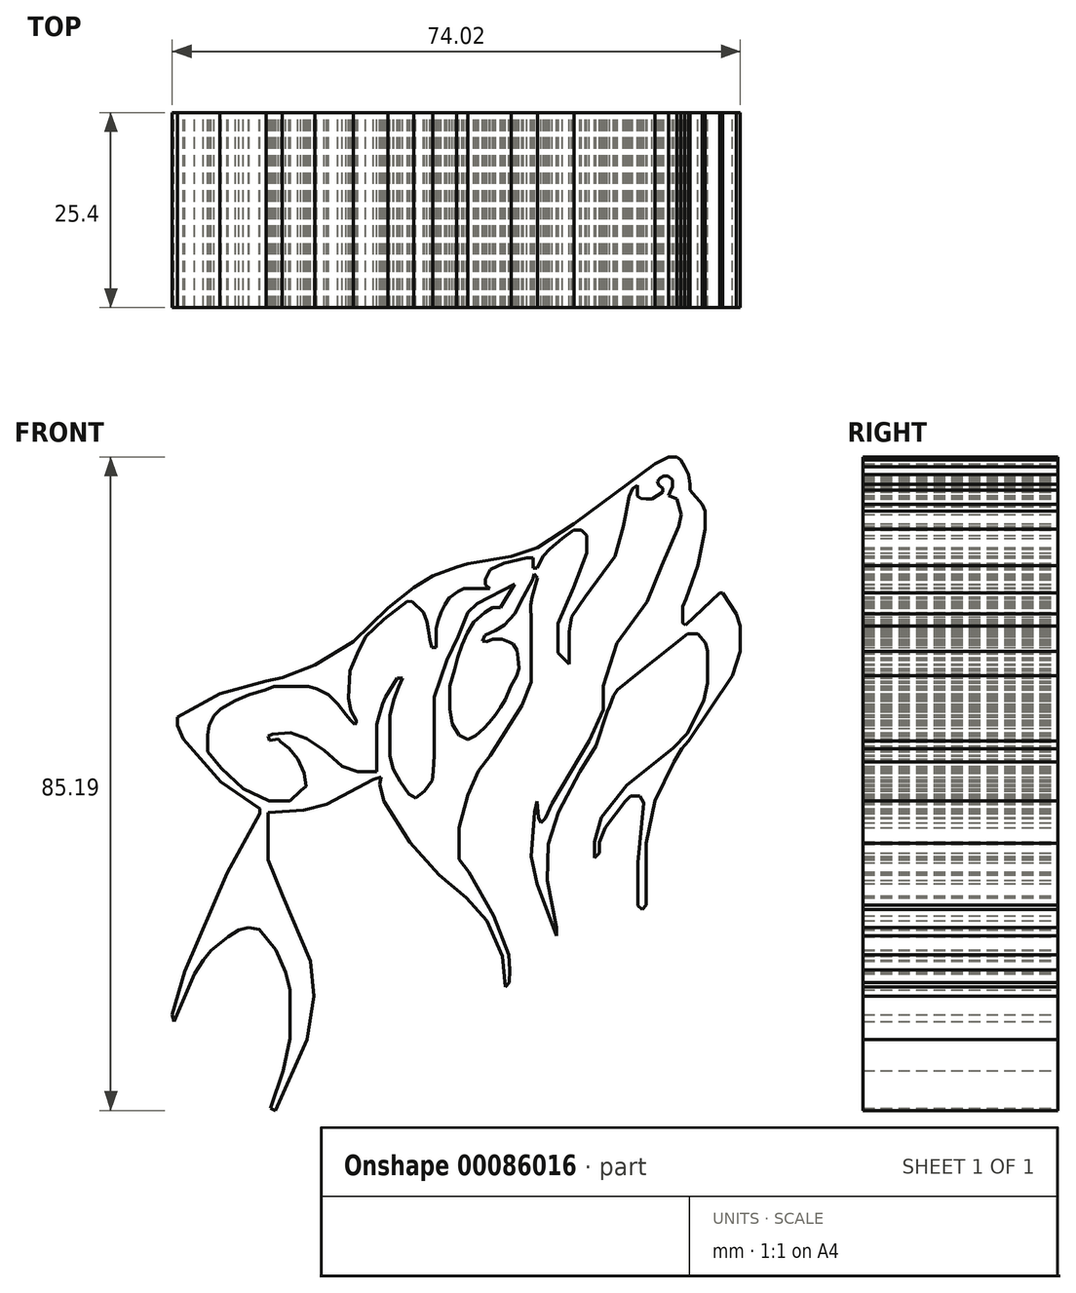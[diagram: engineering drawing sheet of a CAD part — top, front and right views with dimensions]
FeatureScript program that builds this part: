
annotation { "Feature Type Name" : "Feature", "Feature Type Description" : "" }
export const myFeature = defineFeature(function(context is Context, id is Id, definition is map)
    precondition{}
    {
        {
            var Q0;
            Q0=qCreatedBy(makeId("Front.planeOp"),FACE);
            var sketch = newSketch(context, id + "F0", { "sketchPlane" : qUnion([Q0])});
            skLineSegment(sketch, "E0", {"start": v(-38.5, -15.53) * mm, "end": v(-36.88, -9.84) * mm});
            skLineSegment(sketch, "E1", {"start": v(-36.88, -9.84) * mm, "end": v(-31.3, 2.95) * mm});
            skLineSegment(sketch, "E2", {"start": v(-31.3, 2.95) * mm, "end": v(-27.1, 10.73) * mm});
            skLineSegment(sketch, "E3", {"start": v(-27.1, 10.73) * mm, "end": v(-27.1, 11.36) * mm});
            skLineSegment(sketch, "E4", {"start": v(-27.1, 11.36) * mm, "end": v(-32.14, 14.82) * mm});
            skLineSegment(sketch, "E5", {"start": v(-32.14, 14.82) * mm, "end": v(-37.06, 20.41) * mm});
            skLineSegment(sketch, "E6", {"start": v(-37.06, 20.41) * mm, "end": v(-37.8, 22.21) * mm});
            skLineSegment(sketch, "E7", {"start": v(-37.8, 22.21) * mm, "end": v(-37.8, 23.3) * mm});
            skLineSegment(sketch, "E8", {"start": v(-37.8, 23.3) * mm, "end": v(-32.31, 26.36) * mm});
            skLineSegment(sketch, "E9", {"start": v(-32.31, 26.36) * mm, "end": v(-26.28, 28) * mm});
            skLineSegment(sketch, "E10", {"start": v(-26.28, 28) * mm, "end": v(-24.14, 28.41) * mm});
            skLineSegment(sketch, "E11", {"start": v(-24.14, 28.41) * mm, "end": v(-19.93, 30.06) * mm});
            skLineSegment(sketch, "E12", {"start": v(-19.93, 30.06) * mm, "end": v(-14.86, 33.12) * mm});
            skLineSegment(sketch, "E13", {"start": v(-14.86, 33.12) * mm, "end": v(-10.37, 37.53) * mm});
            skLineSegment(sketch, "E14", {"start": v(-10.37, 37.53) * mm, "end": v(-7.02, 40.16) * mm});
            skLineSegment(sketch, "E15", {"start": v(-7.02, 40.16) * mm, "end": v(-4.55, 41.68) * mm});
            skLineSegment(sketch, "E16", {"start": v(-4.55, 41.68) * mm, "end": v(-1.43, 42.86) * mm});
            skLineSegment(sketch, "E17", {"start": v(-1.43, 42.86) * mm, "end": v(0, 43.31) * mm});
            skLineSegment(sketch, "E18", {"start": v(0, 43.31) * mm, "end": v(5.68, 44.23) * mm});
            skLineSegment(sketch, "E19", {"start": v(5.68, 44.23) * mm, "end": v(9.13, 45.4) * mm});
            skLineSegment(sketch, "E20", {"start": v(9.13, 45.4) * mm, "end": v(13.88, 48.46) * mm});
            skLineSegment(sketch, "E21", {"start": v(13.88, 48.46) * mm, "end": v(24.44, 56.3) * mm});
            skLineSegment(sketch, "E22", {"start": v(24.44, 56.3) * mm, "end": v(26.17, 57.2) * mm});
            skLineSegment(sketch, "E23", {"start": v(26.17, 57.2) * mm, "end": v(27.25, 57.2) * mm});
            skLineSegment(sketch, "E24", {"start": v(27.25, 57.2) * mm, "end": v(27.75, 56.8) * mm});
            skLineSegment(sketch, "E25", {"start": v(27.75, 56.8) * mm, "end": v(28.27, 55.93) * mm});
            skLineSegment(sketch, "E26", {"start": v(28.27, 55.93) * mm, "end": v(28.77, 54.9) * mm});
            skLineSegment(sketch, "E27", {"start": v(28.77, 54.9) * mm, "end": v(28.96, 53.66) * mm});
            skLineSegment(sketch, "E28", {"start": v(28.96, 53.66) * mm, "end": v(28.96, 52.88) * mm});
            skLineSegment(sketch, "E29", {"start": v(28.96, 52.88) * mm, "end": v(30.55, 51) * mm});
            skLineSegment(sketch, "E30", {"start": v(30.55, 51) * mm, "end": v(30.97, 50.12) * mm});
            skLineSegment(sketch, "E31", {"start": v(30.97, 50.12) * mm, "end": v(30.97, 47.77) * mm});
            skLineSegment(sketch, "E32", {"start": v(30.97, 47.77) * mm, "end": v(30, 43.06) * mm});
            skLineSegment(sketch, "E33", {"start": v(30, 43.06) * mm, "end": v(28.46, 38.73) * mm});
            skLineSegment(sketch, "E34", {"start": v(28.46, 38.73) * mm, "end": v(28.05, 37.7) * mm});
            skLineSegment(sketch, "E35", {"start": v(28.05, 37.7) * mm, "end": v(28.05, 36.88) * mm});
            skLineSegment(sketch, "E36", {"start": v(28.05, 36.88) * mm, "end": v(28.05, 35.54) * mm});
            skLineSegment(sketch, "E37", {"start": v(28.05, 35.54) * mm, "end": v(28.4, 35.26) * mm});
            skLineSegment(sketch, "E38", {"start": v(28.4, 35.26) * mm, "end": v(32.85, 39.46) * mm});
            skLineSegment(sketch, "E39", {"start": v(32.85, 39.46) * mm, "end": v(33.27, 39.46) * mm});
            skLineSegment(sketch, "E40", {"start": v(33.27, 39.46) * mm, "end": v(35.03, 36.78) * mm});
            skLineSegment(sketch, "E41", {"start": v(35.03, 36.78) * mm, "end": v(35.53, 35.19) * mm});
            skLineSegment(sketch, "E42", {"start": v(35.53, 35.19) * mm, "end": v(35.53, 31.87) * mm});
            skLineSegment(sketch, "E43", {"start": v(35.53, 31.87) * mm, "end": v(34.48, 28.7) * mm});
            skLineSegment(sketch, "E44", {"start": v(34.48, 28.7) * mm, "end": v(32.17, 25.26) * mm});
            skLineSegment(sketch, "E45", {"start": v(32.17, 25.26) * mm, "end": v(28.77, 20.2) * mm});
            skLineSegment(sketch, "E46", {"start": v(28.77, 20.2) * mm, "end": v(27.93, 19.14) * mm});
            skLineSegment(sketch, "E47", {"start": v(27.93, 19.14) * mm, "end": v(26.86, 17.45) * mm});
            skLineSegment(sketch, "E48", {"start": v(26.86, 17.45) * mm, "end": v(24.38, 12.35) * mm});
            skLineSegment(sketch, "E49", {"start": v(24.38, 12.35) * mm, "end": v(23.84, 9.71) * mm});
            skLineSegment(sketch, "E50", {"start": v(23.84, 9.71) * mm, "end": v(23.24, 6.84) * mm});
            skLineSegment(sketch, "E51", {"start": v(23.24, 6.84) * mm, "end": v(23.24, 5.26) * mm});
            skLineSegment(sketch, "E52", {"start": v(23.24, 5.26) * mm, "end": v(23.24, -1.23) * mm});
            skLineSegment(sketch, "E53", {"start": v(23.24, -1.23) * mm, "end": v(22.78, -1.77) * mm});
            skLineSegment(sketch, "E54", {"start": v(22.78, -1.77) * mm, "end": v(22.22, -1.3) * mm});
            skLineSegment(sketch, "E55", {"start": v(22.22, -1.3) * mm, "end": v(22.22, 4.3) * mm});
            skLineSegment(sketch, "E56", {"start": v(22.22, 4.3) * mm, "end": v(22.95, 12.08) * mm});
            skLineSegment(sketch, "E57", {"start": v(22.95, 12.08) * mm, "end": v(22.46, 13) * mm});
            skLineSegment(sketch, "E58", {"start": v(22.46, 13) * mm, "end": v(21.22, 13) * mm});
            skLineSegment(sketch, "E59", {"start": v(21.22, 13) * mm, "end": v(20.51, 12.3) * mm});
            skLineSegment(sketch, "E60", {"start": v(20.51, 12.3) * mm, "end": v(17.91, 8.84) * mm});
            skLineSegment(sketch, "E61", {"start": v(17.91, 8.84) * mm, "end": v(17.16, 6.94) * mm});
            skLineSegment(sketch, "E62", {"start": v(17.16, 6.94) * mm, "end": v(17.16, 5.54) * mm});
            skLineSegment(sketch, "E63", {"start": v(17.16, 5.54) * mm, "end": v(16.56, 4.94) * mm});
            skLineSegment(sketch, "E64", {"start": v(16.56, 4.94) * mm, "end": v(16.56, 7) * mm});
            skLineSegment(sketch, "E65", {"start": v(16.56, 7) * mm, "end": v(17.43, 10.2) * mm});
            skLineSegment(sketch, "E66", {"start": v(17.43, 10.2) * mm, "end": v(20.73, 14.41) * mm});
            skLineSegment(sketch, "E67", {"start": v(20.73, 14.41) * mm, "end": v(26.84, 19.28) * mm});
            skLineSegment(sketch, "E68", {"start": v(26.84, 19.28) * mm, "end": v(28.6, 21.13) * mm});
            skLineSegment(sketch, "E69", {"start": v(28.6, 21.13) * mm, "end": v(30.76, 25.4) * mm});
            skLineSegment(sketch, "E70", {"start": v(30.76, 25.4) * mm, "end": v(31.3, 27.72) * mm});
            skLineSegment(sketch, "E71", {"start": v(31.3, 27.72) * mm, "end": v(31.3, 29.81) * mm});
            skLineSegment(sketch, "E72", {"start": v(31.3, 29.81) * mm, "end": v(31.3, 31.88) * mm});
            skLineSegment(sketch, "E73", {"start": v(31.3, 31.88) * mm, "end": v(31.02, 32.96) * mm});
            skLineSegment(sketch, "E74", {"start": v(31.02, 32.96) * mm, "end": v(29.98, 34.12) * mm});
            skLineSegment(sketch, "E75", {"start": v(29.98, 34.12) * mm, "end": v(28.64, 34.12) * mm});
            skLineSegment(sketch, "E76", {"start": v(28.64, 34.12) * mm, "end": v(22.17, 29.01) * mm});
            skLineSegment(sketch, "E77", {"start": v(22.17, 29.01) * mm, "end": v(19.53, 26.84) * mm});
            skLineSegment(sketch, "E78", {"start": v(19.53, 26.84) * mm, "end": v(19.02, 26.1) * mm});
            skLineSegment(sketch, "E79", {"start": v(19.02, 26.1) * mm, "end": v(18.48, 24.67) * mm});
            skLineSegment(sketch, "E80", {"start": v(18.48, 24.67) * mm, "end": v(18.18, 24) * mm});
            skLineSegment(sketch, "E81", {"start": v(18.18, 24) * mm, "end": v(17.67, 24.23) * mm});
            skLineSegment(sketch, "E82", {"start": v(17.67, 24.23) * mm, "end": v(17.67, 27.37) * mm});
            skLineSegment(sketch, "E83", {"start": v(17.67, 27.37) * mm, "end": v(19.45, 32.92) * mm});
            skLineSegment(sketch, "E84", {"start": v(19.45, 32.92) * mm, "end": v(23.42, 38.36) * mm});
            skLineSegment(sketch, "E85", {"start": v(23.42, 38.36) * mm, "end": v(25.3, 43.03) * mm});
            skLineSegment(sketch, "E86", {"start": v(25.3, 43.03) * mm, "end": v(27.5, 48.16) * mm});
            skLineSegment(sketch, "E87", {"start": v(27.5, 48.16) * mm, "end": v(27.86, 49.72) * mm});
            skLineSegment(sketch, "E88", {"start": v(27.86, 49.72) * mm, "end": v(27.25, 51.74) * mm});
            skLineSegment(sketch, "E89", {"start": v(27.25, 51.74) * mm, "end": v(26.17, 52.2) * mm});
            skLineSegment(sketch, "E90", {"start": v(26.17, 52.2) * mm, "end": v(26.35, 52.6) * mm});
            skLineSegment(sketch, "E91", {"start": v(26.35, 52.6) * mm, "end": v(26.7, 53.3) * mm});
            skLineSegment(sketch, "E92", {"start": v(26.7, 53.3) * mm, "end": v(26.7, 54.22) * mm});
            skLineSegment(sketch, "E93", {"start": v(26.7, 54.22) * mm, "end": v(26.15, 54.7) * mm});
            skLineSegment(sketch, "E94", {"start": v(26.15, 54.7) * mm, "end": v(25.56, 54.7) * mm});
            skLineSegment(sketch, "E95", {"start": v(25.56, 54.7) * mm, "end": v(25.08, 54.48) * mm});
            skLineSegment(sketch, "E96", {"start": v(25.08, 54.48) * mm, "end": v(24.72, 54.04) * mm});
            skLineSegment(sketch, "E97", {"start": v(24.72, 54.04) * mm, "end": v(24.94, 53.52) * mm});
            skLineSegment(sketch, "E98", {"start": v(24.94, 53.52) * mm, "end": v(25.42, 53.15) * mm});
            skLineSegment(sketch, "E99", {"start": v(25.42, 53.15) * mm, "end": v(25.42, 52.6) * mm});
            skLineSegment(sketch, "E100", {"start": v(25.42, 52.6) * mm, "end": v(24.01, 51.72) * mm});
            skLineSegment(sketch, "E101", {"start": v(24.01, 51.72) * mm, "end": v(23.28, 51.72) * mm});
            skLineSegment(sketch, "E102", {"start": v(23.28, 51.72) * mm, "end": v(22.54, 51.79) * mm});
            skLineSegment(sketch, "E103", {"start": v(22.54, 51.79) * mm, "end": v(22.13, 52.12) * mm});
            skLineSegment(sketch, "E104", {"start": v(22.13, 52.12) * mm, "end": v(22.1, 52.86) * mm});
            skLineSegment(sketch, "E105", {"start": v(22.1, 52.86) * mm, "end": v(22.1, 53.52) * mm});
            skLineSegment(sketch, "E106", {"start": v(22.1, 53.52) * mm, "end": v(21.47, 53.04) * mm});
            skLineSegment(sketch, "E107", {"start": v(21.47, 53.04) * mm, "end": v(21.03, 52.05) * mm});
            skLineSegment(sketch, "E108", {"start": v(21.03, 52.05) * mm, "end": v(20.8, 50.72) * mm});
            skLineSegment(sketch, "E109", {"start": v(20.8, 50.72) * mm, "end": v(20.62, 49.72) * mm});
            skLineSegment(sketch, "E110", {"start": v(20.62, 49.72) * mm, "end": v(20.29, 48.1) * mm});
            skLineSegment(sketch, "E111", {"start": v(20.29, 48.1) * mm, "end": v(19.22, 44.27) * mm});
            skLineSegment(sketch, "E112", {"start": v(19.22, 44.27) * mm, "end": v(15.35, 38.95) * mm});
            skLineSegment(sketch, "E113", {"start": v(15.35, 38.95) * mm, "end": v(13.54, 36.37) * mm});
            skLineSegment(sketch, "E114", {"start": v(13.54, 36.37) * mm, "end": v(13.2, 34.38) * mm});
            skLineSegment(sketch, "E115", {"start": v(13.2, 34.38) * mm, "end": v(13.2, 31.28) * mm});
            skLineSegment(sketch, "E116", {"start": v(13.2, 31.28) * mm, "end": v(13.2, 30.2) * mm});
            skLineSegment(sketch, "E117", {"start": v(13.2, 30.2) * mm, "end": v(11.8, 31.65) * mm});
            skLineSegment(sketch, "E118", {"start": v(11.8, 31.65) * mm, "end": v(11.8, 35.45) * mm});
            skLineSegment(sketch, "E119", {"start": v(11.8, 35.45) * mm, "end": v(13.79, 40.15) * mm});
            skLineSegment(sketch, "E120", {"start": v(13.79, 40.15) * mm, "end": v(15.55, 44.66) * mm});
            skLineSegment(sketch, "E121", {"start": v(15.55, 44.66) * mm, "end": v(15.55, 46.96) * mm});
            skLineSegment(sketch, "E122", {"start": v(15.55, 46.96) * mm, "end": v(14.81, 47.7) * mm});
            skLineSegment(sketch, "E123", {"start": v(14.81, 47.7) * mm, "end": v(13.78, 47.7) * mm});
            skLineSegment(sketch, "E124", {"start": v(13.78, 47.7) * mm, "end": v(12.37, 46.56) * mm});
            skLineSegment(sketch, "E125", {"start": v(12.37, 46.56) * mm, "end": v(10.73, 45.2) * mm});
            skLineSegment(sketch, "E126", {"start": v(10.73, 45.2) * mm, "end": v(9.88, 44.3) * mm});
            skLineSegment(sketch, "E127", {"start": v(9.88, 44.3) * mm, "end": v(9.03, 42.71) * mm});
            skLineSegment(sketch, "E128", {"start": v(9.03, 42.71) * mm, "end": v(8.56, 42.71) * mm});
            skLineSegment(sketch, "E129", {"start": v(8.56, 42.71) * mm, "end": v(8.56, 44.03) * mm});
            skLineSegment(sketch, "E130", {"start": v(8.56, 44.03) * mm, "end": v(7.72, 44.03) * mm});
            skLineSegment(sketch, "E131", {"start": v(7.72, 44.03) * mm, "end": v(4.71, 43.37) * mm});
            skLineSegment(sketch, "E132", {"start": v(4.71, 43.37) * mm, "end": v(2.98, 42.53) * mm});
            skLineSegment(sketch, "E133", {"start": v(2.98, 42.53) * mm, "end": v(2.32, 41.26) * mm});
            skLineSegment(sketch, "E134", {"start": v(2.32, 41.26) * mm, "end": v(2.32, 40.55) * mm});
            skLineSegment(sketch, "E135", {"start": v(2.32, 40.55) * mm, "end": v(2.88, 40.04) * mm});
            skLineSegment(sketch, "E136", {"start": v(2.88, 40.04) * mm, "end": v(-0.45, 40.04) * mm});
            skLineSegment(sketch, "E137", {"start": v(-0.45, 40.04) * mm, "end": v(-1.26, 39.64) * mm});
            skLineSegment(sketch, "E138", {"start": v(-1.26, 39.64) * mm, "end": v(-2.36, 38.86) * mm});
            skLineSegment(sketch, "E139", {"start": v(-2.36, 38.86) * mm, "end": v(-2.95, 37.97) * mm});
            skLineSegment(sketch, "E140", {"start": v(-2.95, 37.97) * mm, "end": v(-3.5, 36.97) * mm});
            skLineSegment(sketch, "E141", {"start": v(-3.5, 36.97) * mm, "end": v(-3.86, 35.84) * mm});
            skLineSegment(sketch, "E142", {"start": v(-3.86, 35.84) * mm, "end": v(-4.08, 34.86) * mm});
            skLineSegment(sketch, "E143", {"start": v(-4.08, 34.86) * mm, "end": v(-4.08, 33.83) * mm});
            skLineSegment(sketch, "E144", {"start": v(-4.08, 33.83) * mm, "end": v(-4.08, 32.35) * mm});
            skLineSegment(sketch, "E145", {"start": v(-4.08, 32.35) * mm, "end": v(-4.65, 32.35) * mm});
            skLineSegment(sketch, "E146", {"start": v(-4.65, 32.35) * mm, "end": v(-4.92, 33.36) * mm});
            skLineSegment(sketch, "E147", {"start": v(-4.92, 33.36) * mm, "end": v(-5.14, 34.64) * mm});
            skLineSegment(sketch, "E148", {"start": v(-5.14, 34.64) * mm, "end": v(-5.33, 35.72) * mm});
            skLineSegment(sketch, "E149", {"start": v(-5.33, 35.72) * mm, "end": v(-5.73, 36.97) * mm});
            skLineSegment(sketch, "E150", {"start": v(-5.73, 36.97) * mm, "end": v(-7.2, 38.34) * mm});
            skLineSegment(sketch, "E151", {"start": v(-7.2, 38.34) * mm, "end": v(-7.86, 38.37) * mm});
            skLineSegment(sketch, "E152", {"start": v(-7.86, 38.37) * mm, "end": v(-10.93, 36.06) * mm});
            skLineSegment(sketch, "E153", {"start": v(-10.93, 36.06) * mm, "end": v(-13.28, 33.75) * mm});
            skLineSegment(sketch, "E154", {"start": v(-13.28, 33.75) * mm, "end": v(-14.4, 31.5) * mm});
            skLineSegment(sketch, "E155", {"start": v(-14.4, 31.5) * mm, "end": v(-15.3, 29.3) * mm});
            skLineSegment(sketch, "E156", {"start": v(-15.3, 29.3) * mm, "end": v(-15.54, 25.76) * mm});
            skLineSegment(sketch, "E157", {"start": v(-15.54, 25.76) * mm, "end": v(-15.24, 24.1) * mm});
            skLineSegment(sketch, "E158", {"start": v(-15.24, 24.1) * mm, "end": v(-14.54, 22.83) * mm});
            skLineSegment(sketch, "E159", {"start": v(-14.54, 22.83) * mm, "end": v(-14.54, 22.53) * mm});
            skLineSegment(sketch, "E160", {"start": v(-14.54, 22.53) * mm, "end": v(-14.72, 22.34) * mm});
            skLineSegment(sketch, "E161", {"start": v(-14.72, 22.34) * mm, "end": v(-15.27, 22.9) * mm});
            skLineSegment(sketch, "E162", {"start": v(-15.27, 22.9) * mm, "end": v(-15.87, 23.63) * mm});
            skLineSegment(sketch, "E163", {"start": v(-15.87, 23.63) * mm, "end": v(-16.93, 24.97) * mm});
            skLineSegment(sketch, "E164", {"start": v(-16.93, 24.97) * mm, "end": v(-18.1, 26.2) * mm});
            skLineSegment(sketch, "E165", {"start": v(-18.1, 26.2) * mm, "end": v(-19.67, 26.98) * mm});
            skLineSegment(sketch, "E166", {"start": v(-19.67, 26.98) * mm, "end": v(-20.73, 27.29) * mm});
            skLineSegment(sketch, "E167", {"start": v(-20.73, 27.29) * mm, "end": v(-25.27, 27.29) * mm});
            skLineSegment(sketch, "E168", {"start": v(-25.27, 27.29) * mm, "end": v(-26.35, 26.84) * mm});
            skLineSegment(sketch, "E169", {"start": v(-26.35, 26.84) * mm, "end": v(-28.49, 26.19) * mm});
            skLineSegment(sketch, "E170", {"start": v(-28.49, 26.19) * mm, "end": v(-30.24, 25.44) * mm});
            skLineSegment(sketch, "E171", {"start": v(-30.24, 25.44) * mm, "end": v(-32.14, 24.4) * mm});
            skLineSegment(sketch, "E172", {"start": v(-32.14, 24.4) * mm, "end": v(-33.05, 23.5) * mm});
            skLineSegment(sketch, "E173", {"start": v(-33.05, 23.5) * mm, "end": v(-33.66, 22.2) * mm});
            skLineSegment(sketch, "E174", {"start": v(-33.66, 22.2) * mm, "end": v(-33.87, 20.9) * mm});
            skLineSegment(sketch, "E175", {"start": v(-33.87, 20.9) * mm, "end": v(-33.87, 18.78) * mm});
            skLineSegment(sketch, "E176", {"start": v(-33.87, 18.78) * mm, "end": v(-32.1, 16.6) * mm});
            skLineSegment(sketch, "E177", {"start": v(-32.1, 16.6) * mm, "end": v(-29.22, 13.93) * mm});
            skLineSegment(sketch, "E178", {"start": v(-29.22, 13.93) * mm, "end": v(-25.87, 12.36) * mm});
            skLineSegment(sketch, "E179", {"start": v(-25.87, 12.36) * mm, "end": v(-23.13, 12.36) * mm});
            skLineSegment(sketch, "E180", {"start": v(-23.13, 12.36) * mm, "end": v(-21.76, 13.72) * mm});
            skLineSegment(sketch, "E181", {"start": v(-21.76, 13.72) * mm, "end": v(-21.08, 14.27) * mm});
            skLineSegment(sketch, "E182", {"start": v(-21.08, 14.27) * mm, "end": v(-21.29, 15.98) * mm});
            skLineSegment(sketch, "E183", {"start": v(-21.29, 15.98) * mm, "end": v(-22.1, 17.83) * mm});
            skLineSegment(sketch, "E184", {"start": v(-22.1, 17.83) * mm, "end": v(-23.27, 19.2) * mm});
            skLineSegment(sketch, "E185", {"start": v(-23.27, 19.2) * mm, "end": v(-24.36, 20.02) * mm});
            skLineSegment(sketch, "E186", {"start": v(-24.36, 20.02) * mm, "end": v(-24.7, 20.43) * mm});
            skLineSegment(sketch, "E187", {"start": v(-24.7, 20.43) * mm, "end": v(-25.8, 20.22) * mm});
            skLineSegment(sketch, "E188", {"start": v(-25.8, 20.22) * mm, "end": v(-26, 20.84) * mm});
            skLineSegment(sketch, "E189", {"start": v(-26, 20.84) * mm, "end": v(-25.4, 21.03) * mm});
            skLineSegment(sketch, "E190", {"start": v(-25.4, 21.03) * mm, "end": v(-23.06, 21.25) * mm});
            skLineSegment(sketch, "E191", {"start": v(-23.06, 21.25) * mm, "end": v(-21.01, 20.5) * mm});
            skLineSegment(sketch, "E192", {"start": v(-21.01, 20.5) * mm, "end": v(-18.69, 18.99) * mm});
            skLineSegment(sketch, "E193", {"start": v(-18.69, 18.99) * mm, "end": v(-16.36, 16.87) * mm});
            skLineSegment(sketch, "E194", {"start": v(-16.36, 16.87) * mm, "end": v(-14.3, 16.19) * mm});
            skLineSegment(sketch, "E195", {"start": v(-14.3, 16.19) * mm, "end": v(-12.67, 16.19) * mm});
            skLineSegment(sketch, "E196", {"start": v(-12.67, 16.19) * mm, "end": v(-11.85, 16.19) * mm});
            skLineSegment(sketch, "E197", {"start": v(-11.85, 16.19) * mm, "end": v(-11.85, 18.86) * mm});
            skLineSegment(sketch, "E198", {"start": v(-11.85, 18.86) * mm, "end": v(-11.83, 20.73) * mm});
            skLineSegment(sketch, "E199", {"start": v(-11.83, 20.73) * mm, "end": v(-11.83, 22.32) * mm});
            skLineSegment(sketch, "E200", {"start": v(-11.83, 22.32) * mm, "end": v(-11.51, 23.5) * mm});
            skLineSegment(sketch, "E201", {"start": v(-11.51, 23.5) * mm, "end": v(-11.1, 25) * mm});
            skLineSegment(sketch, "E202", {"start": v(-11.1, 25) * mm, "end": v(-10.67, 25.9) * mm});
            skLineSegment(sketch, "E203", {"start": v(-10.67, 25.9) * mm, "end": v(-9.16, 28.35) * mm});
            skLineSegment(sketch, "E204", {"start": v(-9.16, 28.35) * mm, "end": v(-8.5, 28.35) * mm});
            skLineSegment(sketch, "E205", {"start": v(-8.5, 28.35) * mm, "end": v(-9, 27.23) * mm});
            skLineSegment(sketch, "E206", {"start": v(-9, 27.23) * mm, "end": v(-9.6, 25.55) * mm});
            skLineSegment(sketch, "E207", {"start": v(-9.6, 25.55) * mm, "end": v(-10.12, 23.47) * mm});
            skLineSegment(sketch, "E208", {"start": v(-10.12, 23.47) * mm, "end": v(-10.12, 19.92) * mm});
            skLineSegment(sketch, "E209", {"start": v(-10.12, 19.92) * mm, "end": v(-10.12, 18.2) * mm});
            skLineSegment(sketch, "E210", {"start": v(-10.12, 18.2) * mm, "end": v(-9.66, 16.47) * mm});
            skLineSegment(sketch, "E211", {"start": v(-9.66, 16.47) * mm, "end": v(-8.8, 14.9) * mm});
            skLineSegment(sketch, "E212", {"start": v(-8.8, 14.9) * mm, "end": v(-7.68, 13.27) * mm});
            skLineSegment(sketch, "E213", {"start": v(-7.68, 13.27) * mm, "end": v(-6.77, 12.72) * mm});
            skLineSegment(sketch, "E214", {"start": v(-6.77, 12.72) * mm, "end": v(-5.65, 13.63) * mm});
            skLineSegment(sketch, "E215", {"start": v(-5.65, 13.63) * mm, "end": v(-4.59, 15.05) * mm});
            skLineSegment(sketch, "E216", {"start": v(-4.59, 15.05) * mm, "end": v(-4.48, 16.22) * mm});
            skLineSegment(sketch, "E217", {"start": v(-4.48, 16.22) * mm, "end": v(-4.33, 18.35) * mm});
            skLineSegment(sketch, "E218", {"start": v(-4.33, 18.35) * mm, "end": v(-4.33, 23.37) * mm});
            skLineSegment(sketch, "E219", {"start": v(-4.33, 23.37) * mm, "end": v(-4.33, 25.9) * mm});
            skLineSegment(sketch, "E220", {"start": v(-4.33, 25.9) * mm, "end": v(-2.7, 30.73) * mm});
            skLineSegment(sketch, "E221", {"start": v(-2.7, 30.73) * mm, "end": v(-1.26, 33.75) * mm});
            skLineSegment(sketch, "E222", {"start": v(-1.26, 33.75) * mm, "end": v(0, 36.92) * mm});
            skLineSegment(sketch, "E223", {"start": v(0, 36.92) * mm, "end": v(1.24, 38.1) * mm});
            skLineSegment(sketch, "E224", {"start": v(1.24, 38.1) * mm, "end": v(6.12, 40.6) * mm});
            skLineSegment(sketch, "E225", {"start": v(6.12, 40.6) * mm, "end": v(4.28, 37.57) * mm});
            skLineSegment(sketch, "E226", {"start": v(4.28, 37.57) * mm, "end": v(3.24, 37.57) * mm});
            skLineSegment(sketch, "E227", {"start": v(3.24, 37.57) * mm, "end": v(2.27, 36.96) * mm});
            skLineSegment(sketch, "E228", {"start": v(2.27, 36.96) * mm, "end": v(0.76, 35.7) * mm});
            skLineSegment(sketch, "E229", {"start": v(0.76, 35.7) * mm, "end": v(-0.06, 34.29) * mm});
            skLineSegment(sketch, "E230", {"start": v(-0.06, 34.29) * mm, "end": v(-0.74, 32.69) * mm});
            skLineSegment(sketch, "E231", {"start": v(-0.74, 32.69) * mm, "end": v(-1.32, 31.04) * mm});
            skLineSegment(sketch, "E232", {"start": v(-1.32, 31.04) * mm, "end": v(-1.71, 29.48) * mm});
            skLineSegment(sketch, "E233", {"start": v(-1.71, 29.48) * mm, "end": v(-2.3, 27.35) * mm});
            skLineSegment(sketch, "E234", {"start": v(-2.3, 27.35) * mm, "end": v(-2.3, 24.39) * mm});
            skLineSegment(sketch, "E235", {"start": v(-2.3, 24.39) * mm, "end": v(-2, 22.4) * mm});
            skLineSegment(sketch, "E236", {"start": v(-2, 22.4) * mm, "end": v(-1.13, 20.94) * mm});
            skLineSegment(sketch, "E237", {"start": v(-1.13, 20.94) * mm, "end": v(0, 20.36) * mm});
            skLineSegment(sketch, "E238", {"start": v(0, 20.36) * mm, "end": v(1.05, 20.9) * mm});
            skLineSegment(sketch, "E239", {"start": v(1.05, 20.9) * mm, "end": v(2.12, 21.82) * mm});
            skLineSegment(sketch, "E240", {"start": v(2.12, 21.82) * mm, "end": v(2.8, 22.6) * mm});
            skLineSegment(sketch, "E241", {"start": v(2.8, 22.6) * mm, "end": v(3.63, 23.61) * mm});
            skLineSegment(sketch, "E242", {"start": v(3.63, 23.61) * mm, "end": v(4.26, 24.54) * mm});
            skLineSegment(sketch, "E243", {"start": v(4.26, 24.54) * mm, "end": v(4.94, 25.55) * mm});
            skLineSegment(sketch, "E244", {"start": v(4.94, 25.55) * mm, "end": v(5.62, 27.25) * mm});
            skLineSegment(sketch, "E245", {"start": v(5.62, 27.25) * mm, "end": v(6.4, 28.61) * mm});
            skLineSegment(sketch, "E246", {"start": v(6.4, 28.61) * mm, "end": v(6.68, 29.63) * mm});
            skLineSegment(sketch, "E247", {"start": v(6.68, 29.63) * mm, "end": v(6.59, 30.94) * mm});
            skLineSegment(sketch, "E248", {"start": v(6.59, 30.94) * mm, "end": v(6.44, 31.96) * mm});
            skLineSegment(sketch, "E249", {"start": v(6.44, 31.96) * mm, "end": v(5.9, 32.78) * mm});
            skLineSegment(sketch, "E250", {"start": v(5.9, 32.78) * mm, "end": v(5.42, 33.08) * mm});
            skLineSegment(sketch, "E251", {"start": v(5.42, 33.08) * mm, "end": v(4.5, 33.42) * mm});
            skLineSegment(sketch, "E252", {"start": v(4.5, 33.42) * mm, "end": v(3.24, 33.42) * mm});
            skLineSegment(sketch, "E253", {"start": v(3.24, 33.42) * mm, "end": v(2.5, 33.12) * mm});
            skLineSegment(sketch, "E254", {"start": v(2.5, 33.12) * mm, "end": v(1.93, 33.22) * mm});
            skLineSegment(sketch, "E255", {"start": v(1.93, 33.22) * mm, "end": v(2.27, 33.95) * mm});
            skLineSegment(sketch, "E256", {"start": v(2.27, 33.95) * mm, "end": v(3.63, 34.58) * mm});
            skLineSegment(sketch, "E257", {"start": v(3.63, 34.58) * mm, "end": v(4.8, 35.3) * mm});
            skLineSegment(sketch, "E258", {"start": v(4.8, 35.3) * mm, "end": v(6.15, 36.76) * mm});
            skLineSegment(sketch, "E259", {"start": v(6.15, 36.76) * mm, "end": v(7.27, 38.95) * mm});
            skLineSegment(sketch, "E260", {"start": v(7.27, 38.95) * mm, "end": v(8.48, 41.18) * mm});
            skLineSegment(sketch, "E261", {"start": v(8.48, 41.18) * mm, "end": v(8.67, 41.96) * mm});
            skLineSegment(sketch, "E262", {"start": v(8.67, 41.96) * mm, "end": v(9.1, 41.42) * mm});
            skLineSegment(sketch, "E263", {"start": v(9.1, 41.42) * mm, "end": v(8.43, 39) * mm});
            skLineSegment(sketch, "E264", {"start": v(8.43, 39) * mm, "end": v(8.19, 37.88) * mm});
            skLineSegment(sketch, "E265", {"start": v(8.19, 37.88) * mm, "end": v(8.28, 35.8) * mm});
            skLineSegment(sketch, "E266", {"start": v(8.28, 35.8) * mm, "end": v(8.28, 27.88) * mm});
            skLineSegment(sketch, "E267", {"start": v(8.28, 27.88) * mm, "end": v(7.07, 24.83) * mm});
            skLineSegment(sketch, "E268", {"start": v(7.07, 24.83) * mm, "end": v(2.95, 18.28) * mm});
            skLineSegment(sketch, "E269", {"start": v(2.95, 18.28) * mm, "end": v(1.44, 16.29) * mm});
            skLineSegment(sketch, "E270", {"start": v(1.44, 16.29) * mm, "end": v(0, 13.1) * mm});
            skLineSegment(sketch, "E271", {"start": v(0, 13.1) * mm, "end": v(-1.11, 8.88) * mm});
            skLineSegment(sketch, "E272", {"start": v(-1.11, 8.88) * mm, "end": v(-1.11, 4.77) * mm});
            skLineSegment(sketch, "E273", {"start": v(-1.11, 4.77) * mm, "end": v(0.17, 3.1) * mm});
            skLineSegment(sketch, "E274", {"start": v(0.17, 3.1) * mm, "end": v(3.37, -2.63) * mm});
            skLineSegment(sketch, "E275", {"start": v(3.37, -2.63) * mm, "end": v(5.36, -7.73) * mm});
            skLineSegment(sketch, "E276", {"start": v(5.36, -7.73) * mm, "end": v(5.48, -9.66) * mm});
            skLineSegment(sketch, "E277", {"start": v(5.48, -9.66) * mm, "end": v(5.42, -11.33) * mm});
            skLineSegment(sketch, "E278", {"start": v(5.42, -11.33) * mm, "end": v(4.92, -11.89) * mm});
            skLineSegment(sketch, "E279", {"start": v(4.92, -11.89) * mm, "end": v(4.55, -7.92) * mm});
            skLineSegment(sketch, "E280", {"start": v(4.55, -7.92) * mm, "end": v(2.5, -3.26) * mm});
            skLineSegment(sketch, "E281", {"start": v(2.5, -3.26) * mm, "end": v(-0.16, -0.29) * mm});
            skLineSegment(sketch, "E282", {"start": v(-0.16, -0.29) * mm, "end": v(-3.7, 2.7) * mm});
            skLineSegment(sketch, "E283", {"start": v(-3.7, 2.7) * mm, "end": v(-7.55, 6.98) * mm});
            skLineSegment(sketch, "E284", {"start": v(-7.55, 6.98) * mm, "end": v(-10.9, 12.31) * mm});
            skLineSegment(sketch, "E285", {"start": v(-10.9, 12.31) * mm, "end": v(-11.46, 14.55) * mm});
            skLineSegment(sketch, "E286", {"start": v(-11.46, 14.55) * mm, "end": v(-11.27, 15.48) * mm});
            skLineSegment(sketch, "E287", {"start": v(-11.27, 15.48) * mm, "end": v(-12.27, 15.17) * mm});
            skLineSegment(sketch, "E288", {"start": v(-12.27, 15.17) * mm, "end": v(-18.4, 11.94) * mm});
            skLineSegment(sketch, "E289", {"start": v(-18.4, 11.94) * mm, "end": v(-21.39, 11.13) * mm});
            skLineSegment(sketch, "E290", {"start": v(-21.39, 11.13) * mm, "end": v(-26, 10.84) * mm});
            skLineSegment(sketch, "E291", {"start": v(-26, 10.84) * mm, "end": v(-26, 9.5) * mm});
            skLineSegment(sketch, "E292", {"start": v(-26, 9.5) * mm, "end": v(-26, 7.8) * mm});
            skLineSegment(sketch, "E293", {"start": v(-26, 7.8) * mm, "end": v(-26, 4.68) * mm});
            skLineSegment(sketch, "E294", {"start": v(-26, 4.68) * mm, "end": v(-24.08, 0) * mm});
            skLineSegment(sketch, "E295", {"start": v(-24.08, 0) * mm, "end": v(-20.46, -8.54) * mm});
            skLineSegment(sketch, "E296", {"start": v(-20.46, -8.54) * mm, "end": v(-20.02, -13.13) * mm});
            skLineSegment(sketch, "E297", {"start": v(-20.02, -13.13) * mm, "end": v(-20.95, -18.78) * mm});
            skLineSegment(sketch, "E298", {"start": v(-20.95, -18.78) * mm, "end": v(-25.07, -28) * mm});
            skLineSegment(sketch, "E299", {"start": v(-25.07, -28) * mm, "end": v(-25.67, -27.73) * mm});
            skLineSegment(sketch, "E300", {"start": v(-25.67, -27.73) * mm, "end": v(-24.04, -22.84) * mm});
            skLineSegment(sketch, "E301", {"start": v(-24.04, -22.84) * mm, "end": v(-23.18, -18.65) * mm});
            skLineSegment(sketch, "E302", {"start": v(-23.18, -18.65) * mm, "end": v(-23.18, -12.26) * mm});
            skLineSegment(sketch, "E303", {"start": v(-23.18, -12.26) * mm, "end": v(-23.74, -10.02) * mm});
            skLineSegment(sketch, "E304", {"start": v(-23.74, -10.02) * mm, "end": v(-25.02, -7.08) * mm});
            skLineSegment(sketch, "E305", {"start": v(-25.02, -7.08) * mm, "end": v(-27.12, -4.4) * mm});
            skLineSegment(sketch, "E306", {"start": v(-27.12, -4.4) * mm, "end": v(-28.55, -4.17) * mm});
            skLineSegment(sketch, "E307", {"start": v(-28.55, -4.17) * mm, "end": v(-29.84, -4.45) * mm});
            skLineSegment(sketch, "E308", {"start": v(-29.84, -4.45) * mm, "end": v(-31.22, -5.36) * mm});
            skLineSegment(sketch, "E309", {"start": v(-31.22, -5.36) * mm, "end": v(-33.42, -7.13) * mm});
            skLineSegment(sketch, "E310", {"start": v(-33.42, -7.13) * mm, "end": v(-34.47, -8.41) * mm});
            skLineSegment(sketch, "E311", {"start": v(-34.47, -8.41) * mm, "end": v(-35.61, -10.18) * mm});
            skLineSegment(sketch, "E312", {"start": v(-35.61, -10.18) * mm, "end": v(-38.23, -16.38) * mm});
            skLineSegment(sketch, "E313", {"start": v(-38.23, -16.38) * mm, "end": v(-38.5, -15.53) * mm});
            skLineSegment(sketch, "E314", {"start": v(17.67, 24.23) * mm, "end": v(15.83, 20.15) * mm});
            skLineSegment(sketch, "E315", {"start": v(15.83, 20.15) * mm, "end": v(11.04, 12.07) * mm});
            skLineSegment(sketch, "E316", {"start": v(11.04, 12.07) * mm, "end": v(10.1, 10.06) * mm});
            skLineSegment(sketch, "E317", {"start": v(10.1, 10.06) * mm, "end": v(9.54, 9.53) * mm});
            skLineSegment(sketch, "E318", {"start": v(9.54, 9.53) * mm, "end": v(9.23, 10.2) * mm});
            skLineSegment(sketch, "E319", {"start": v(9.23, 10.2) * mm, "end": v(9.05, 12.32) * mm});
            skLineSegment(sketch, "E320", {"start": v(9.05, 12.32) * mm, "end": v(8.74, 10.88) * mm});
            skLineSegment(sketch, "E321", {"start": v(8.74, 10.88) * mm, "end": v(8.28, 5.1) * mm});
            skLineSegment(sketch, "E322", {"start": v(8.28, 5.1) * mm, "end": v(9.05, 1.58) * mm});
            skLineSegment(sketch, "E323", {"start": v(9.05, 1.58) * mm, "end": v(11.58, -5.26) * mm});
            skLineSegment(sketch, "E324", {"start": v(11.58, -5.26) * mm, "end": v(11.58, -4.12) * mm});
            skLineSegment(sketch, "E325", {"start": v(11.58, -4.12) * mm, "end": v(10.35, 2) * mm});
            skLineSegment(sketch, "E326", {"start": v(10.35, 2) * mm, "end": v(10.53, 6.72) * mm});
            skLineSegment(sketch, "E327", {"start": v(10.53, 6.72) * mm, "end": v(11.84, 10.9) * mm});
            skLineSegment(sketch, "E328", {"start": v(11.84, 10.9) * mm, "end": v(14.64, 16.15) * mm});
            skLineSegment(sketch, "E329", {"start": v(14.64, 16.15) * mm, "end": v(16.73, 19.56) * mm});
            skLineSegment(sketch, "E330", {"start": v(16.73, 19.56) * mm, "end": v(18.18, 24) * mm});
            skSolve(sketch);
        }
        {
            var Q0;
            Q0 = qSketchRegion(id + "F0", true);
            extrude(context, id + "F1", {"entities" : qUnion([Q0]), "depth" : 25.4 * mm});
        }
    });
